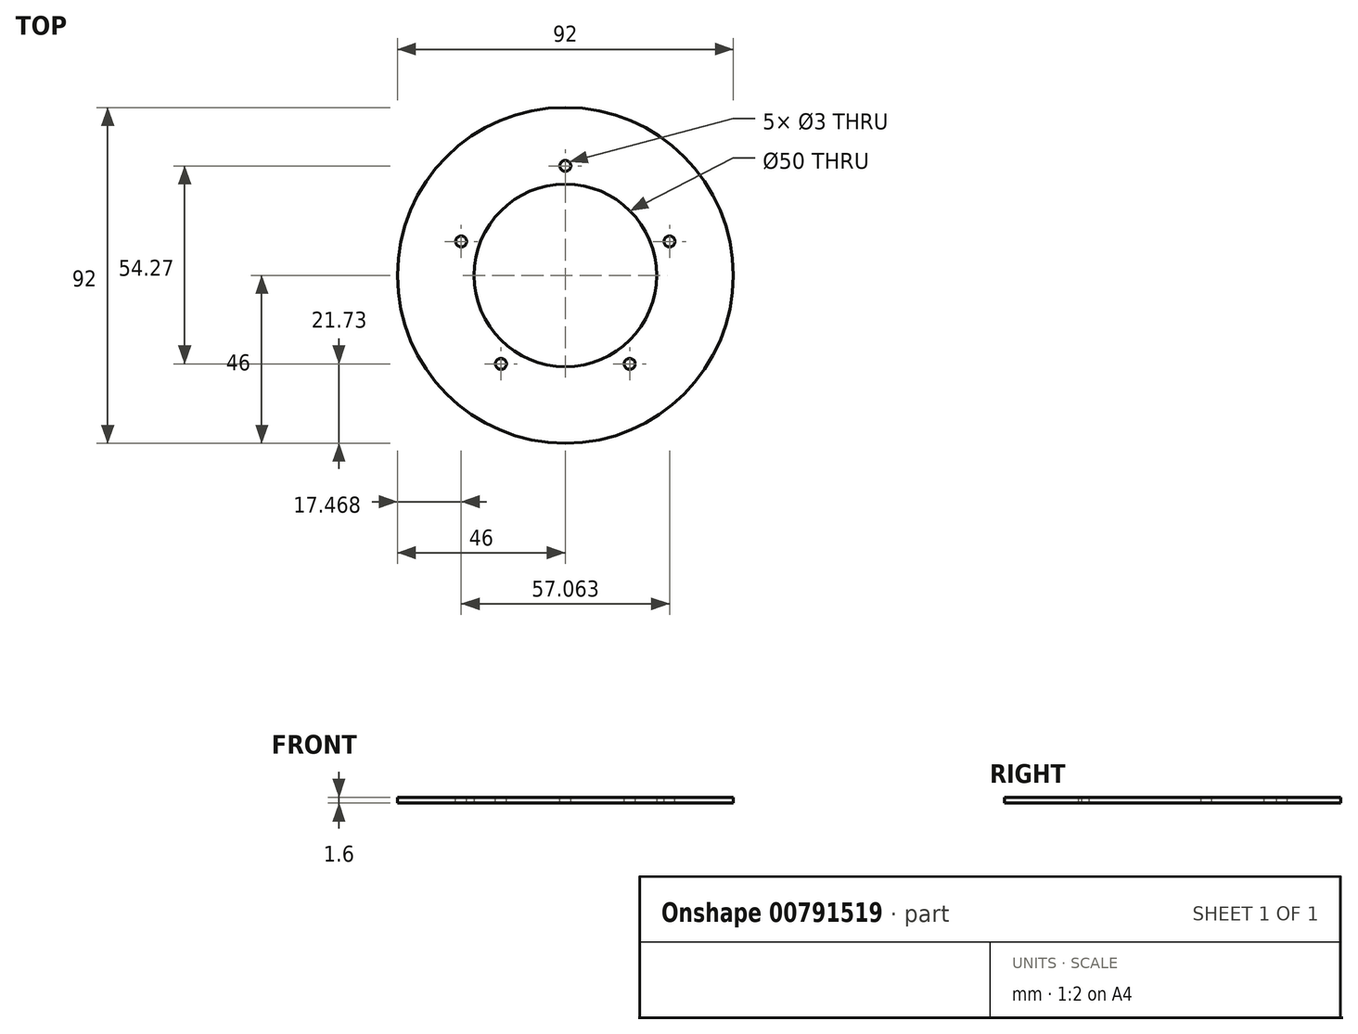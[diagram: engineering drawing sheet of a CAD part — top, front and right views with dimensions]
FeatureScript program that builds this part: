
annotation { "Feature Type Name" : "Feature", "Feature Type Description" : "" }
export const myFeature = defineFeature(function(context is Context, id is Id, definition is map)
    precondition{}
    {
        {
            var Q0;
            Q0=qCreatedBy(makeId("Top.planeOp"),FACE);
            var sketch = newSketch(context, id + "F0", { "sketchPlane" : qUnion([Q0])});
            skCircle(sketch, "E0", {"center": v(0, 0) * mm, "radius": 46 * mm});
            skCircle(sketch, "E1", {"center": v(0, 0) * mm, "radius": 25 * mm});
            skSolve(sketch);
        }
        {
            var Q0;
            Q0 = qSketchRegion(id + "F0", true);
            extrude(context, id + "F1", {"entities" : qUnion([Q0]), "depth" : 1.6 * mm, "offsetDistance" : 25.4 * mm});
        }
        {
            var Q0;
            Q0=makeQuery(id+"F1.opExtrude","CAP_FACE",FACE,{"disambiguationData":[OSD([sQuery(id+"F0.wireOp",EDGE,"E0"),sQuery(id+"F0.wireOp",EDGE,"E1")])],"isStart":false});
            var sketch = newSketch(context, id + "F2", { "sketchPlane" : qUnion([Q0])});
            skCircle(sketch, "E2", {"center": v(0, 30) * mm, "radius": 1.5 * mm});
            skCircle(sketch, "E3.1.0", {"center": v(-28.53, 9.27) * mm, "radius": 1.5 * mm});
            skCircle(sketch, "E3.2.0", {"center": v(-17.63, -24.27) * mm, "radius": 1.5 * mm});
            skCircle(sketch, "E3.3.0", {"center": v(17.63, -24.27) * mm, "radius": 1.5 * mm});
            skCircle(sketch, "E3.4.0", {"center": v(28.53, 9.27) * mm, "radius": 1.5 * mm});
            skPoint(sketch, "E3.center", {"position": v(0, 0) * mm});
            skSolve(sketch);
        }
        {
            var Q0;
            Q0 = qSketchRegion(id + "F2", true);
            extrude(context, id + "F3", {"entities" : qUnion([Q0]), "operationType" : NewBodyOperationType.REMOVE, "oppositeDirection" : true, "depth" : 25.4 * mm, "offsetDistance" : 25.4 * mm});
        }
    });
